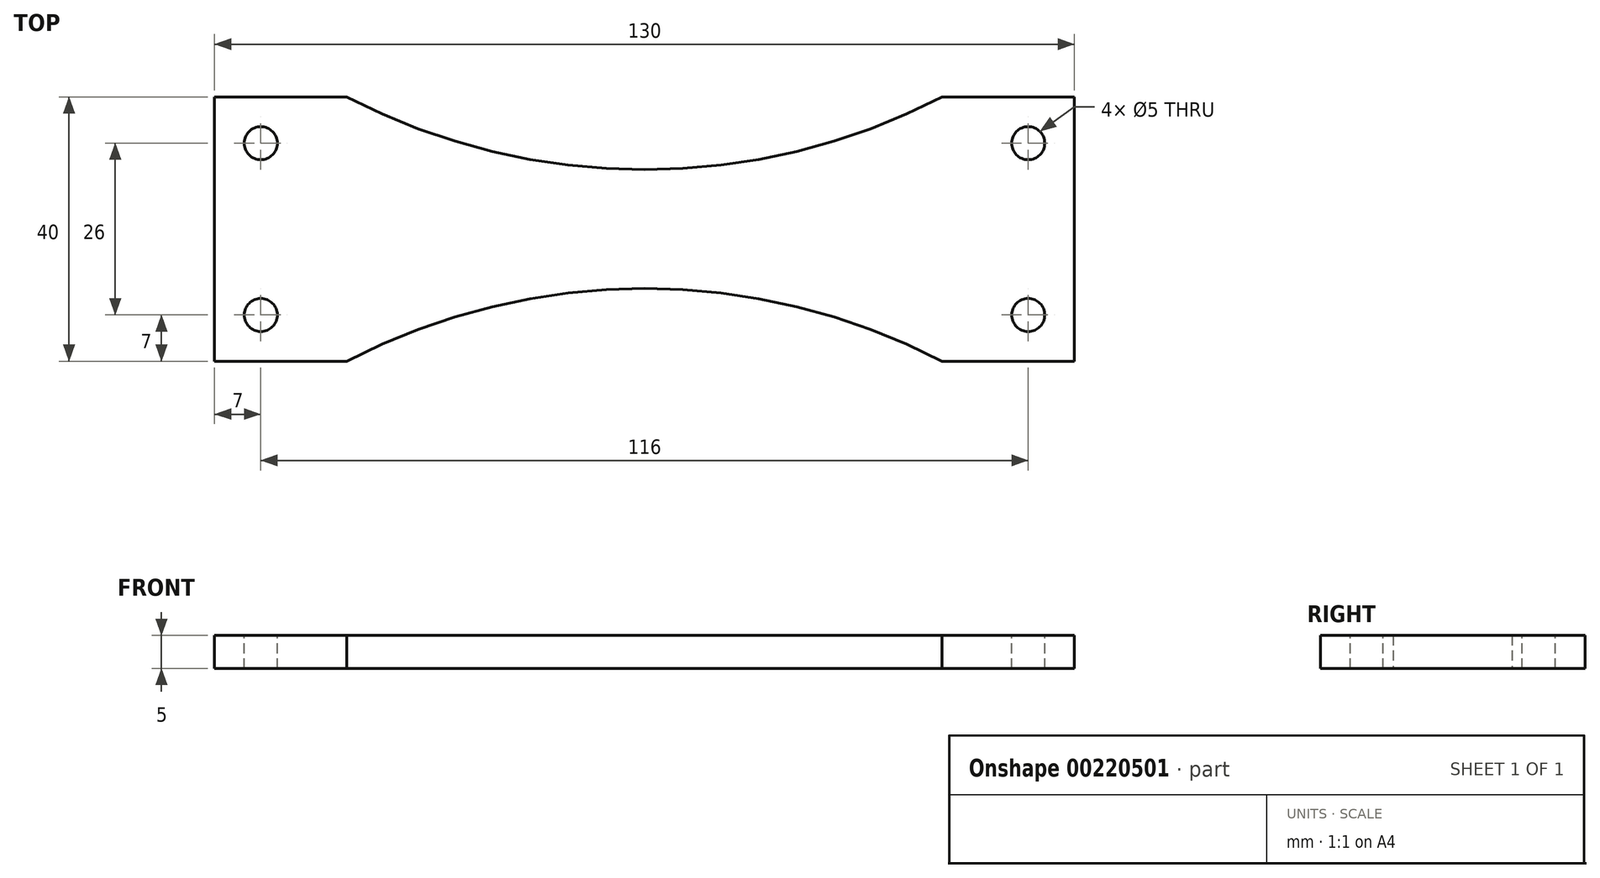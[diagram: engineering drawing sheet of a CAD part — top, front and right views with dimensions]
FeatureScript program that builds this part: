
annotation { "Feature Type Name" : "Feature", "Feature Type Description" : "" }
export const myFeature = defineFeature(function(context is Context, id is Id, definition is map)
    precondition{}
    {
        {
            var Q0;
            Q0=qCreatedBy(makeId("Top.planeOp"),FACE);
            var sketch = newSketch(context, id + "F0", { "sketchPlane" : qUnion([Q0])});
            skLineSegment(sketch, "E0.left", {"start": v(-65, 20) * mm, "end": v(-65, -20) * mm});
            skLineSegment(sketch, "E0.right", {"start": v(65, 20) * mm, "end": v(65, -20) * mm});
            skArc(sketch, "E1", {"start": v(45, -20) * mm, "mid": v(0, -9) * mm, "end": v(-45, -20) * mm});
            skArc(sketch, "E2", {"start": v(-45, 20) * mm, "mid": v(0, 9) * mm, "end": v(45, 20) * mm});
            skLineSegment(sketch, "E3", {"start": v(-65, -20) * mm, "end": v(-45, -20) * mm});
            skLineSegment(sketch, "E4", {"start": v(-65, 20) * mm, "end": v(-45, 20) * mm});
            skLineSegment(sketch, "E5", {"start": v(45, 20) * mm, "end": v(65, 20) * mm});
            skLineSegment(sketch, "E6", {"start": v(65, -20) * mm, "end": v(45, -20) * mm});
            skSolve(sketch);
        }
        {
            var Q0;
            Q0 = qSketchRegion(id + "F0", true);
            extrude(context, id + "F1", {"entities" : qUnion([Q0]), "depth" : 5 * mm});
        }
        {
            var Q0;
            Q0=makeQuery(id+"F1.opExtrude","CAP_FACE",FACE,{"disambiguationData":[OSD([sQuery(id+"F0.wireOp",EDGE,"E0.left"),sQuery(id+"F0.wireOp",EDGE,"E0.right"),sQuery(id+"F0.wireOp",EDGE,"E1"),sQuery(id+"F0.wireOp",EDGE,"E2"),sQuery(id+"F0.wireOp",EDGE,"E3"),sQuery(id+"F0.wireOp",EDGE,"E4"),sQuery(id+"F0.wireOp",EDGE,"E5"),sQuery(id+"F0.wireOp",EDGE,"E6")])],"isStart":false});
            var sketch = newSketch(context, id + "F2", { "sketchPlane" : qUnion([Q0])});
            skCircle(sketch, "E7", {"center": v(-58, 13) * mm, "radius": 2.5 * mm});
            skCircle(sketch, "E8.0.1.0", {"center": v(-58, -13) * mm, "radius": 2.5 * mm});
            skCircle(sketch, "E8.1.0.0", {"center": v(58, 13) * mm, "radius": 2.5 * mm});
            skCircle(sketch, "E8.1.1.0", {"center": v(58, -13) * mm, "radius": 2.5 * mm});
            skLineSegment(sketch, "E8.direction1", {"start": v(-58, 13) * mm, "end": v(58, 13) * mm, "construction": true});
            skLineSegment(sketch, "E8.direction2", {"start": v(-58, 13) * mm, "end": v(-58, -13) * mm, "construction": true});
            skSolve(sketch);
        }
        {
            var Q0;
            Q0 = qSketchRegion(id + "F2", true);
            extrude(context, id + "F3", {"entities" : qUnion([Q0]), "operationType" : NewBodyOperationType.REMOVE, "endBound" : BoundingType.THROUGH_ALL, "oppositeDirection" : true, "depth" : 25 * mm});
        }
    });
